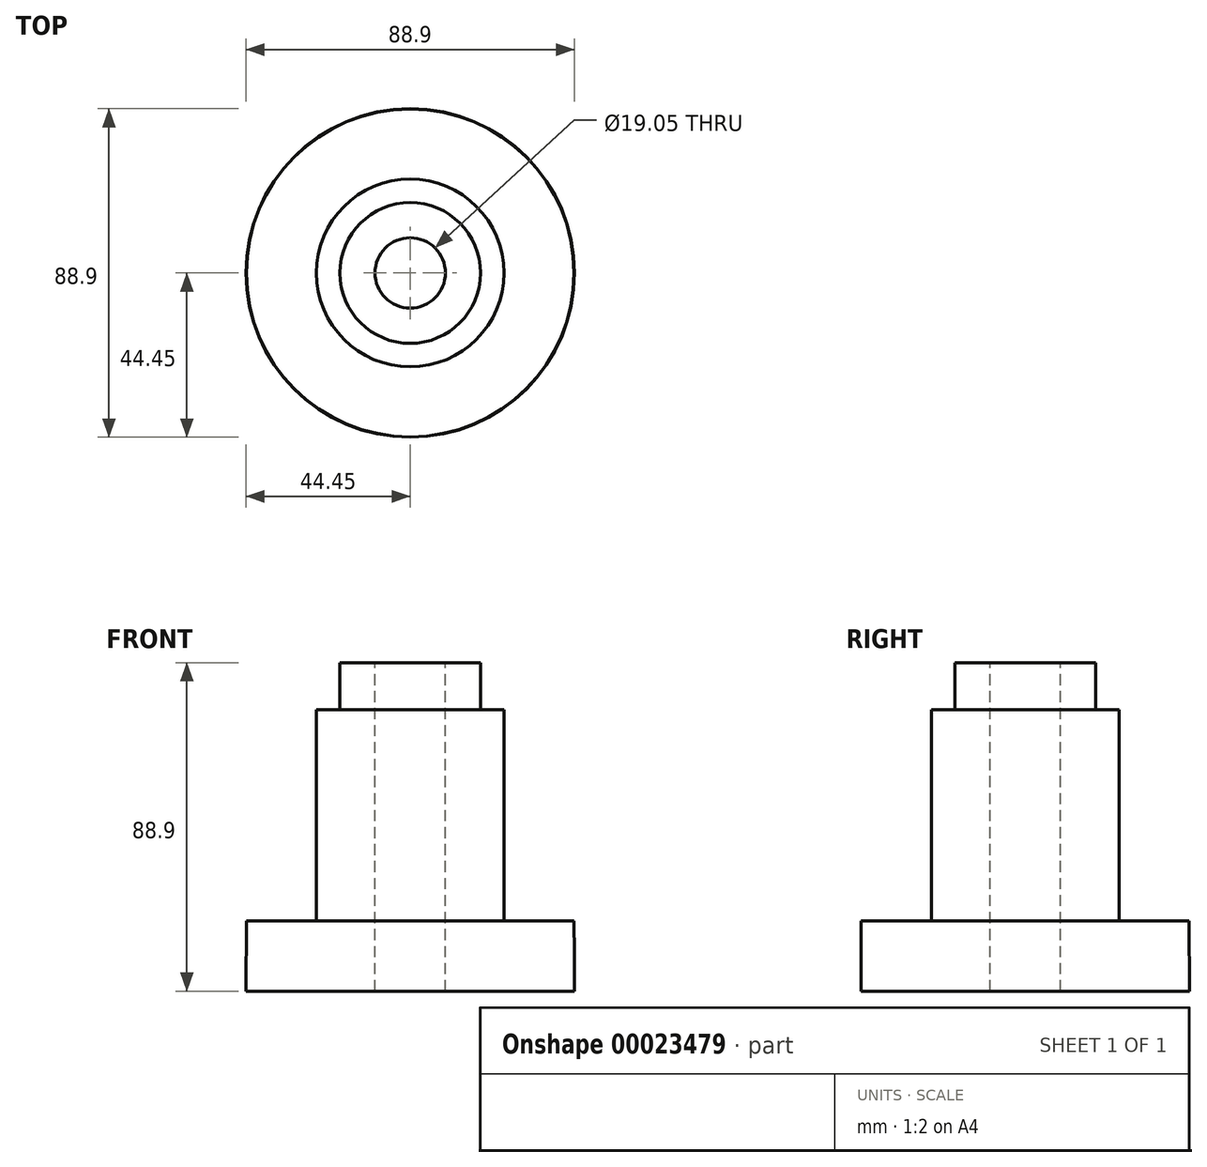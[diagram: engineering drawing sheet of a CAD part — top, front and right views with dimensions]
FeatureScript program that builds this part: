
annotation { "Feature Type Name" : "Feature", "Feature Type Description" : "" }
export const myFeature = defineFeature(function(context is Context, id is Id, definition is map)
    precondition{}
    {
        {
            var Q0;
            Q0=qCreatedBy(makeId("Front.planeOp"),FACE);
            var sketch = newSketch(context, id + "F0", { "sketchPlane" : qUnion([Q0])});
            skLineSegment(sketch, "E0", {"start": v(0, 57.47) * mm, "end": v(0, -57.9) * mm, "construction": true});
            skLineSegment(sketch, "E1", {"start": v(9.53, -57.9) * mm, "end": v(44.45, -57.9) * mm});
            skLineSegment(sketch, "E2", {"start": v(9.53, -57.9) * mm, "end": v(9.53, -38.86) * mm});
            skLineSegment(sketch, "E3", {"start": v(9.53, -38.86) * mm, "end": v(44.36, -38.86) * mm});
            skLineSegment(sketch, "E4", {"start": v(44.36, -38.86) * mm, "end": v(44.45, -57.9) * mm});
            skLineSegment(sketch, "E5.bottom", {"start": v(9.53, -38.86) * mm, "end": v(25.4, -38.86) * mm});
            skLineSegment(sketch, "E5.top", {"start": v(9.53, 18.3) * mm, "end": v(25.4, 18.3) * mm});
            skLineSegment(sketch, "E5.left", {"start": v(9.53, -38.86) * mm, "end": v(9.53, 18.3) * mm});
            skLineSegment(sketch, "E5.right", {"start": v(25.4, -38.86) * mm, "end": v(25.4, 18.3) * mm});
            skLineSegment(sketch, "E6.bottom", {"start": v(9.53, 18.3) * mm, "end": v(19.05, 18.3) * mm});
            skLineSegment(sketch, "E6.top", {"start": v(9.53, 31) * mm, "end": v(19.05, 31) * mm});
            skLineSegment(sketch, "E6.left", {"start": v(9.53, 18.3) * mm, "end": v(9.53, 31) * mm});
            skLineSegment(sketch, "E6.right", {"start": v(19.05, 18.3) * mm, "end": v(19.05, 31) * mm});
            skSolve(sketch);
        }
        {
            var Q0;
            Q0 = qSketchRegion(id + "F0", true);
            var Q1;
            Q1=sQuery(id+"F0.wireOp",EDGE,"E0");
            revolve(context, id + "F1", {"entities" : qUnion([Q0]), "axis" : qUnion([Q1]), "revolveType" : RevolveType.FULL});
        }
    });
